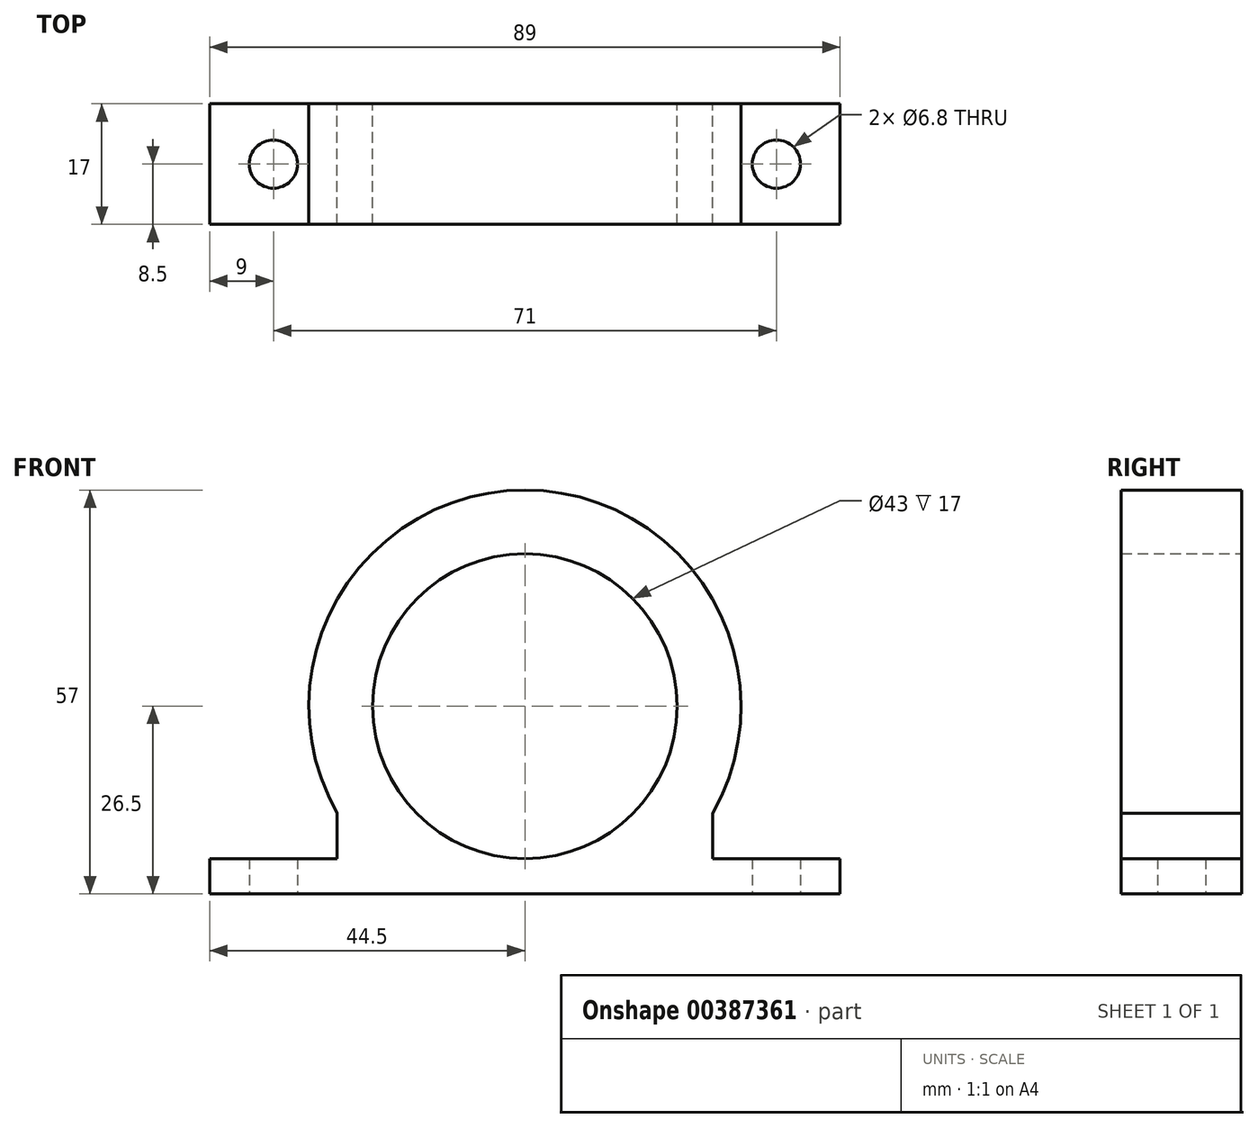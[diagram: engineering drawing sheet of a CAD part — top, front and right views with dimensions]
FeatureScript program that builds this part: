
annotation { "Feature Type Name" : "Feature", "Feature Type Description" : "" }
export const myFeature = defineFeature(function(context is Context, id is Id, definition is map)
    precondition{}
    {
        {
            var Q0;
            Q0=qCreatedBy(makeId("Front.planeOp"),FACE);
            var sketch = newSketch(context, id + "F0", { "sketchPlane" : qUnion([Q0])});
            skCircle(sketch, "E0", {"center": v(0, 0) * mm, "radius": 21.5 * mm});
            skPoint(sketch, "E1", {"position": v(-26.5, 0) * mm});
            skPoint(sketch, "E2", {"position": v(26.5, 0) * mm});
            skPoint(sketch, "E3", {"position": v(0, -26.5) * mm});
            skPoint(sketch, "E4", {"position": v(-26.5, -26.5) * mm});
            skPoint(sketch, "E5", {"position": v(26.5, -26.5) * mm});
            skLineSegment(sketch, "E6", {"start": v(-26.5, -26.5) * mm, "end": v(-35.5, -26.5) * mm, "construction": true});
            skLineSegment(sketch, "E7", {"start": v(26.5, -26.5) * mm, "end": v(35.5, -26.5) * mm, "construction": true});
            skPoint(sketch, "E8", {"position": v(-35.5, -26.5) * mm});
            skPoint(sketch, "E9", {"position": v(35.5, -26.5) * mm});
            skLineSegment(sketch, "E10", {"start": v(-26.5, -26.5) * mm, "end": v(-44.5, -26.5) * mm, "construction": true});
            skLineSegment(sketch, "E11", {"start": v(26.5, -26.5) * mm, "end": v(44.5, -26.5) * mm, "construction": true});
            skPoint(sketch, "E12", {"position": v(-44.5, -26.5) * mm});
            skPoint(sketch, "E13", {"position": v(44.5, -26.5) * mm});
            skLineSegment(sketch, "E14", {"start": v(-44.5, -26.5) * mm, "end": v(-44.5, -21.5) * mm});
            skLineSegment(sketch, "E15", {"start": v(-44.5, -26.5) * mm, "end": v(44.5, -26.5) * mm});
            skLineSegment(sketch, "E16", {"start": v(44.5, -26.5) * mm, "end": v(44.5, -21.5) * mm});
            skLineSegment(sketch, "E17", {"start": v(-44.5, -21.5) * mm, "end": v(-26.5, -21.5) * mm});
            skLineSegment(sketch, "E18", {"start": v(26.5, -21.5) * mm, "end": v(44.5, -21.5) * mm});
            skLineSegment(sketch, "E19", {"start": v(-26.5, 0) * mm, "end": v(26.5, 0) * mm, "construction": true});
            skLineSegment(sketch, "E20", {"start": v(26.5, 0) * mm, "end": v(30.5, 0) * mm, "construction": true});
            skCircle(sketch, "E21", {"center": v(0, 0) * mm, "radius": 30.5 * mm, "construction": true});
            skPoint(sketch, "E22", {"position": v(-26.5, -15.1) * mm});
            skPoint(sketch, "E23", {"position": v(26.5, -15.1) * mm});
            skArc(sketch, "E24", {"start": v(-26.5, -15.1) * mm, "mid": v(0, 30.5) * mm, "end": v(26.5, -15.1) * mm});
            skLineSegment(sketch, "E25", {"start": v(-26.5, -21.5) * mm, "end": v(-26.5, -15.1) * mm});
            skLineSegment(sketch, "E26", {"start": v(26.5, -21.5) * mm, "end": v(26.5, -15.1) * mm});
            skSolve(sketch);
        }
        {
            var Q0;
            Q0=makeQuery(id+"F0.imprint","IMPRINT",FACE,{"disambiguationData":[TD([[makeQuery(id+"F0.imprint","IMPRINT",EDGE,{"derivedFrom":sQuery(id+"F0.wireOp",EDGE,"E0")}),-1.0]])]});
            extrude(context, id + "F1", {"entities" : qUnion([Q0]), "depth" : 17 * mm, "offsetDistance" : 25 * mm});
        }
        {
            var Q0;
            Q0=makeQuery(id+"F1.opExtrude","SWEPT_FACE",FACE,{"disambiguationData":[OSD([sQuery(id+"F0.wireOp",EDGE,"E15")])]});
            var sketch = newSketch(context, id + "F2", { "sketchPlane" : qUnion([Q0])});
            skPoint(sketch, "E27", {"position": v(-44.5, 17) * mm});
            skLineSegment(sketch, "E28", {"start": v(-44.5, 17) * mm, "end": v(-44.5, 8.5) * mm, "construction": true});
            skLineSegment(sketch, "E29", {"start": v(-44.5, 8.5) * mm, "end": v(44.5, 8.5) * mm, "construction": true});
            skLineSegment(sketch, "E30", {"start": v(-44.5, 8.5) * mm, "end": v(-35.5, 8.5) * mm, "construction": true});
            skLineSegment(sketch, "E31", {"start": v(44.5, 8.5) * mm, "end": v(35.5, 8.5) * mm, "construction": true});
            skPoint(sketch, "E32", {"position": v(-35.5, 8.5) * mm});
            skPoint(sketch, "E33", {"position": v(35.5, 8.5) * mm});
            skCircle(sketch, "E34", {"center": v(-35.5, 8.5) * mm, "radius": 3.4 * mm});
            skCircle(sketch, "E35", {"center": v(35.5, 8.5) * mm, "radius": 3.4 * mm});
            skSolve(sketch);
        }
        {
            var Q0;
            Q0=makeQuery(id+"F2.imprint","IMPRINT",FACE,{"disambiguationData":[TD([[makeQuery(id+"F2.imprint","IMPRINT",EDGE,{"derivedFrom":sQuery(id+"F2.wireOp",EDGE,"E34")}),1.0]])]});
            var Q1;
            Q1=makeQuery(id+"F2.imprint","IMPRINT",FACE,{"disambiguationData":[TD([[makeQuery(id+"F2.imprint","IMPRINT",EDGE,{"derivedFrom":sQuery(id+"F2.wireOp",EDGE,"E35")}),1.0]])]});
            extrude(context, id + "F3", {"entities" : qUnion([Q0, Q1]), "operationType" : NewBodyOperationType.REMOVE, "endBound" : BoundingType.THROUGH_ALL, "oppositeDirection" : true, "depth" : 25 * mm, "offsetDistance" : 25 * mm});
        }
    });
